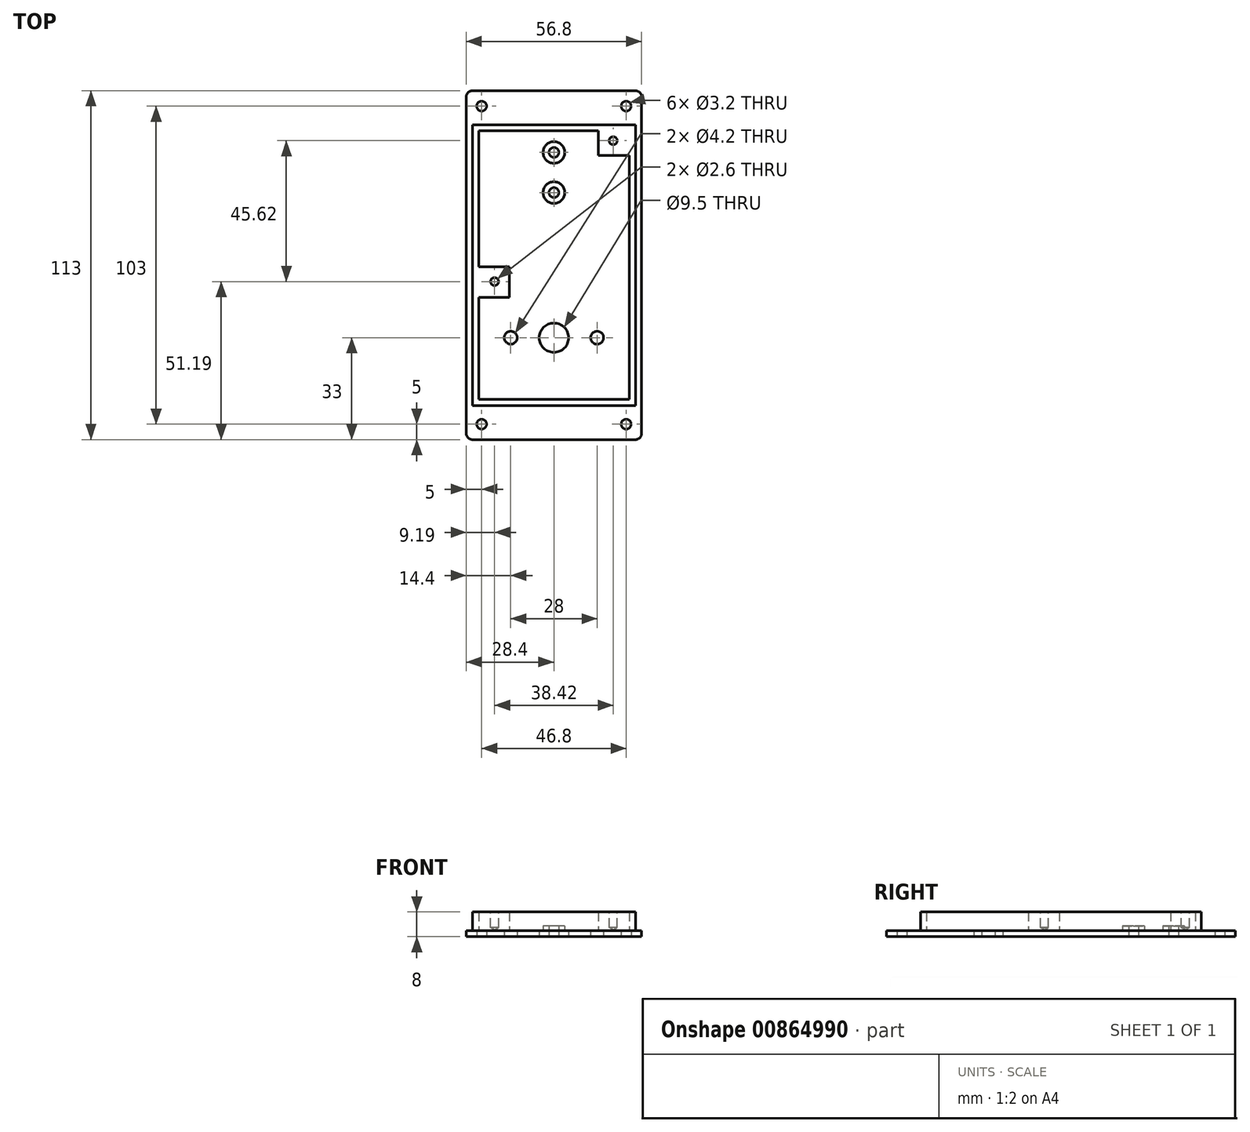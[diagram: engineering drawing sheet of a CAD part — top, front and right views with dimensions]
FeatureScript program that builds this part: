
annotation { "Feature Type Name" : "Feature", "Feature Type Description" : "" }
export const myFeature = defineFeature(function(context is Context, id is Id, definition is map)
    precondition{}
    {
        {
            var Q0;
            Q0=qCreatedBy(makeId("Top.planeOp"),FACE);
            var sketch = newSketch(context, id + "F0", { "sketchPlane" : qUnion([Q0])});
            skLineSegment(sketch, "E0.bottom", {"start": v(26.4, 56.5) * mm, "end": v(-26.4, 56.5) * mm});
            skLineSegment(sketch, "E0.top", {"start": v(26.4, -56.5) * mm, "end": v(-26.4, -56.5) * mm});
            skLineSegment(sketch, "E0.left", {"start": v(28.4, 54.5) * mm, "end": v(28.4, -54.5) * mm});
            skLineSegment(sketch, "E0.right", {"start": v(-28.4, 54.5) * mm, "end": v(-28.4, -54.5) * mm});
            skPoint(sketch, "E0.middle", {"position": v(0, 0) * mm});
            skPoint(sketch, "E1.visualSharp", {"position": v(-28.4, 56.5) * mm});
            skArc(sketch, "E1.filletArc", {"start": v(-26.4, 56.5) * mm, "mid": v(-27.81, 55.91) * mm, "end": v(-28.4, 54.5) * mm});
            skPoint(sketch, "E2.visualSharp", {"position": v(28.4, 56.5) * mm});
            skArc(sketch, "E2.filletArc", {"start": v(28.4, 54.5) * mm, "mid": v(27.81, 55.91) * mm, "end": v(26.4, 56.5) * mm});
            skPoint(sketch, "E3.visualSharp", {"position": v(28.4, -56.5) * mm});
            skArc(sketch, "E3.filletArc", {"start": v(26.4, -56.5) * mm, "mid": v(27.81, -55.91) * mm, "end": v(28.4, -54.5) * mm});
            skPoint(sketch, "E4.visualSharp", {"position": v(-28.4, -56.5) * mm});
            skArc(sketch, "E4.filletArc", {"start": v(-28.4, -54.5) * mm, "mid": v(-27.81, -55.91) * mm, "end": v(-26.4, -56.5) * mm});
            skPoint(sketch, "E5", {"position": v(0, 36.5) * mm});
            skPoint(sketch, "E6", {"position": v(0, 23.5) * mm});
            skPoint(sketch, "E7", {"position": v(-23.4, 51.5) * mm});
            skPoint(sketch, "E8", {"position": v(0, -23.5) * mm});
            skPoint(sketch, "E8.positionSnap0", {"position": v(0, -56.5) * mm});
            skPoint(sketch, "E9", {"position": v(-14, -23.5) * mm});
            skPoint(sketch, "E10", {"position": v(14, -23.5) * mm});
            skPoint(sketch, "E11", {"position": v(23.4, 51.5) * mm});
            skPoint(sketch, "E12", {"position": v(-23.4, -51.5) * mm});
            skPoint(sketch, "E13", {"position": v(23.4, -51.5) * mm});
            skSolve(sketch);
        }
        {
            var Q0;
            Q0=makeQuery(id+"F0.imprint","IMPRINT",FACE,{"disambiguationData":[TD([[makeQuery(id+"F0.imprint","IMPRINT",EDGE,{"derivedFrom":sQuery(id+"F0.wireOp",EDGE,"E0.bottom")}),1.0]])]});
            extrude(context, id + "F1", {"entities" : qUnion([Q0]), "depth" : 2 * mm, "offsetDistance" : 25 * mm});
        }
        {
            var Q0;
            Q0=sQuery(id+"F0.wireOp",VERTEX,"E7");
            var Q1;
            Q1=sQuery(id+"F0.wireOp",VERTEX,"E11");
            var Q2;
            Q2=sQuery(id+"F0.wireOp",VERTEX,"E13");
            var Q3;
            Q3=sQuery(id+"F0.wireOp",VERTEX,"E12");
            var Q4;
            Q4=sQuery(id+"F0.wireOp",VERTEX,"E6");
            var Q5;
            Q5=sQuery(id+"F0.wireOp",VERTEX,"E5");
            var Q6;
            Q6=makeQuery(id+"F1.opExtrude","SWEPT_BODY",BODY,{"disambiguationData":[OSD([sQuery(id+"F0.wireOp",EDGE,"E0.bottom"),sQuery(id+"F0.wireOp",EDGE,"E0.top"),sQuery(id+"F0.wireOp",EDGE,"E0.left"),sQuery(id+"F0.wireOp",EDGE,"E0.right"),sQuery(id+"F0.wireOp",EDGE,"E1.filletArc"),sQuery(id+"F0.wireOp",EDGE,"E2.filletArc"),sQuery(id+"F0.wireOp",EDGE,"E3.filletArc"),sQuery(id+"F0.wireOp",EDGE,"E4.filletArc")])]});
            hole(context, id + "F2", {"style" : HoleStyle.SIMPLE, "endStyle" : HoleEndStyle.THROUGH, "oppositeDirection" : true, "holeDiameter" : 3.2 * mm, "majorDiameter" : 5 * mm, "isTappedThrough" : true, "tappedDepth" : 12 * mm, "tapClearance" : 3, "locations" : qUnion([Q0, Q1, Q2, Q3, Q4, Q5]), "scope" : qUnion([Q6])});
        }
        {
            var Q0;
            Q0=sQuery(id+"F0.wireOp",VERTEX,"E9");
            var Q1;
            Q1=sQuery(id+"F0.wireOp",VERTEX,"E10");
            var Q2;
            Q2=makeQuery(id+"F1.opExtrude","SWEPT_BODY",BODY,{"disambiguationData":[OSD([sQuery(id+"F0.wireOp",EDGE,"E0.bottom"),sQuery(id+"F0.wireOp",EDGE,"E0.top"),sQuery(id+"F0.wireOp",EDGE,"E0.left"),sQuery(id+"F0.wireOp",EDGE,"E0.right"),sQuery(id+"F0.wireOp",EDGE,"E1.filletArc"),sQuery(id+"F0.wireOp",EDGE,"E2.filletArc"),sQuery(id+"F0.wireOp",EDGE,"E3.filletArc"),sQuery(id+"F0.wireOp",EDGE,"E4.filletArc")])]});
            hole(context, id + "F3", {"style" : HoleStyle.SIMPLE, "endStyle" : HoleEndStyle.THROUGH, "oppositeDirection" : true, "holeDiameter" : 4.2 * mm, "majorDiameter" : 5 * mm, "isTappedThrough" : true, "tappedDepth" : 12 * mm, "tapClearance" : 3, "locations" : qUnion([Q0, Q1]), "scope" : qUnion([Q2])});
        }
        {
            var Q0;
            Q0=sQuery(id+"F0.wireOp",VERTEX,"E8");
            var Q1;
            Q1=makeQuery(id+"F1.opExtrude","SWEPT_BODY",BODY,{"disambiguationData":[OSD([sQuery(id+"F0.wireOp",EDGE,"E0.bottom"),sQuery(id+"F0.wireOp",EDGE,"E0.top"),sQuery(id+"F0.wireOp",EDGE,"E0.left"),sQuery(id+"F0.wireOp",EDGE,"E0.right"),sQuery(id+"F0.wireOp",EDGE,"E1.filletArc"),sQuery(id+"F0.wireOp",EDGE,"E2.filletArc"),sQuery(id+"F0.wireOp",EDGE,"E3.filletArc"),sQuery(id+"F0.wireOp",EDGE,"E4.filletArc")])]});
            hole(context, id + "F4", {"style" : HoleStyle.SIMPLE, "endStyle" : HoleEndStyle.THROUGH, "oppositeDirection" : true, "holeDiameter" : 9.5 * mm, "majorDiameter" : 5 * mm, "isTappedThrough" : true, "tappedDepth" : 12 * mm, "tapClearance" : 3, "locations" : qUnion([Q0]), "scope" : qUnion([Q1])});
        }
        {
            var Q0;
            Q0=makeQuery(id+"F1.opExtrude","CAP_FACE",FACE,{"disambiguationData":[OSD([sQuery(id+"F0.wireOp",EDGE,"E0.bottom"),sQuery(id+"F0.wireOp",EDGE,"E0.top"),sQuery(id+"F0.wireOp",EDGE,"E0.left"),sQuery(id+"F0.wireOp",EDGE,"E0.right"),sQuery(id+"F0.wireOp",EDGE,"E1.filletArc"),sQuery(id+"F0.wireOp",EDGE,"E2.filletArc"),sQuery(id+"F0.wireOp",EDGE,"E3.filletArc"),sQuery(id+"F0.wireOp",EDGE,"E4.filletArc")])],"isStart":false});
            var sketch = newSketch(context, id + "F5", { "sketchPlane" : qUnion([Q0])});
            skLineSegment(sketch, "E14", {"start": v(-26.4, 45.5) * mm, "end": v(26.4, 45.5) * mm});
            skLineSegment(sketch, "E15", {"start": v(26.4, 45.5) * mm, "end": v(26.4, -45.5) * mm});
            skLineSegment(sketch, "E16", {"start": v(26.4, -45.5) * mm, "end": v(-26.4, -45.5) * mm});
            skLineSegment(sketch, "E17", {"start": v(-26.4, -45.5) * mm, "end": v(-26.4, 45.5) * mm});
            skLineSegment(sketch, "E18", {"start": v(-24.4, 43.5) * mm, "end": v(24.4, 43.5) * mm});
            skLineSegment(sketch, "E19", {"start": v(24.4, 43.5) * mm, "end": v(24.4, -43.5) * mm});
            skLineSegment(sketch, "E20", {"start": v(24.4, -43.5) * mm, "end": v(-24.4, -43.5) * mm});
            skLineSegment(sketch, "E21", {"start": v(-24.4, -43.5) * mm, "end": v(-24.4, 43.5) * mm});
            skLineSegment(sketch, "E22", {"start": v(-24.4, -0.5) * mm, "end": v(-14.4, -0.5) * mm});
            skLineSegment(sketch, "E23", {"start": v(-14.4, -0.5) * mm, "end": v(-14.4, -10.5) * mm});
            skLineSegment(sketch, "E24", {"start": v(-14.4, -10.5) * mm, "end": v(-24.4, -10.5) * mm});
            skLineSegment(sketch, "E25", {"start": v(14.4, 43.5) * mm, "end": v(14.4, 35.5) * mm});
            skLineSegment(sketch, "E26", {"start": v(14.4, 35.5) * mm, "end": v(24.4, 35.5) * mm});
            skCircle(sketch, "E27", {"center": v(0, 36.5) * mm, "radius": 3.5 * mm});
            skCircle(sketch, "E28", {"center": v(0, 23.5) * mm, "radius": 3.5 * mm});
            skSolve(sketch);
        }
        {
            var Q0;
            Q0=makeQuery(id+"F5.imprint","IMPRINT",FACE,{"disambiguationData":[TD([[makeQuery(id+"F5.imprint","IMPRINT",EDGE,{"derivedFrom":sQuery(id+"F5.wireOp",EDGE,"E14")}),-1.0]])]});
            var Q1;
            {var subQ3=sQuery(id+"F5.wireOp",EDGE,"E25");Q1=makeQuery(id+"F5.imprint","IMPRINT",FACE,{"disambiguationData":[TD([[makeQuery(id+"F5.imprint","IMPRINT",EDGE,{"derivedFrom":subQ3}),1.0]])]});}
            var Q2;
            {var subQ0=sQuery(id+"F5.wireOp",EDGE,"E22");Q2=makeQuery(id+"F5.imprint","IMPRINT",FACE,{"disambiguationData":[TD([[makeQuery(id+"F5.imprint","IMPRINT",EDGE,{"derivedFrom":subQ0}),-1.0]])]});}
            extrude(context, id + "F6", {"entities" : qUnion([Q0, Q1, Q2]), "operationType" : NewBodyOperationType.ADD, "depth" : 6 * mm, "offsetDistance" : 25 * mm});
        }
        {
            var Q0;
            Q0=makeQuery(id+"F6.opExtrude","CAP_FACE",FACE,{"disambiguationData":[OSD([sQuery(id+"F5.wireOp",EDGE,"E14"),sQuery(id+"F5.wireOp",EDGE,"E15"),sQuery(id+"F5.wireOp",EDGE,"E16"),sQuery(id+"F5.wireOp",EDGE,"E17"),sQuery(id+"F5.wireOp",EDGE,"E18"),sQuery(id+"F5.wireOp",EDGE,"E19"),sQuery(id+"F5.wireOp",EDGE,"E20"),sQuery(id+"F5.wireOp",EDGE,"E21"),sQuery(id+"F5.wireOp",EDGE,"E25"),sQuery(id+"F5.wireOp",EDGE,"E26")])],"isStart":false});
            var sketch = newSketch(context, id + "F7", { "sketchPlane" : qUnion([Q0])});
            skPoint(sketch, "E29", {"position": v(19.21, 40.3) * mm});
            skPoint(sketch, "E30", {"position": v(-19.21, -5.31) * mm});
            skSolve(sketch);
        }
        {
            var Q0;
            Q0=sQuery(id+"F7.wireOp",VERTEX,"E30");
            var Q1;
            Q1=sQuery(id+"F7.wireOp",VERTEX,"E29");
            var Q2;
            Q2=makeQuery(id+"F1.opExtrude","SWEPT_BODY",BODY,{"disambiguationData":[OSD([sQuery(id+"F0.wireOp",EDGE,"E0.bottom"),sQuery(id+"F0.wireOp",EDGE,"E0.top"),sQuery(id+"F0.wireOp",EDGE,"E0.left"),sQuery(id+"F0.wireOp",EDGE,"E0.right"),sQuery(id+"F0.wireOp",EDGE,"E1.filletArc"),sQuery(id+"F0.wireOp",EDGE,"E2.filletArc"),sQuery(id+"F0.wireOp",EDGE,"E3.filletArc"),sQuery(id+"F0.wireOp",EDGE,"E4.filletArc")])]});
            hole(context, id + "F8", {"style" : HoleStyle.SIMPLE, "endStyle" : HoleEndStyle.BLIND, "holeDiameter" : 2.6 * mm, "majorDiameter" : 5 * mm, "holeDepth" : 5 * mm, "isTappedThrough" : true, "tappedDepth" : 12 * mm, "tapClearance" : 3, "locations" : qUnion([Q0, Q1]), "scope" : qUnion([Q2])});
        }
        {
            var Q0;
            Q0=makeQuery(id+"F5.imprint","IMPRINT",FACE,{"disambiguationData":[TD([[makeQuery(id+"F5.imprint","IMPRINT",EDGE,{"derivedFrom":sQuery(id+"F5.wireOp",EDGE,"E27")}),1.0]])]});
            var Q1;
            Q1=makeQuery(id+"F5.imprint","IMPRINT",FACE,{"disambiguationData":[TD([[makeQuery(id+"F5.imprint","IMPRINT",EDGE,{"derivedFrom":sQuery(id+"F5.wireOp",EDGE,"E28")}),1.0]])]});
            extrude(context, id + "F9", {"entities" : qUnion([Q0, Q1]), "operationType" : NewBodyOperationType.ADD, "depth" : 1.5 * mm, "offsetDistance" : 25 * mm});
        }
    });
